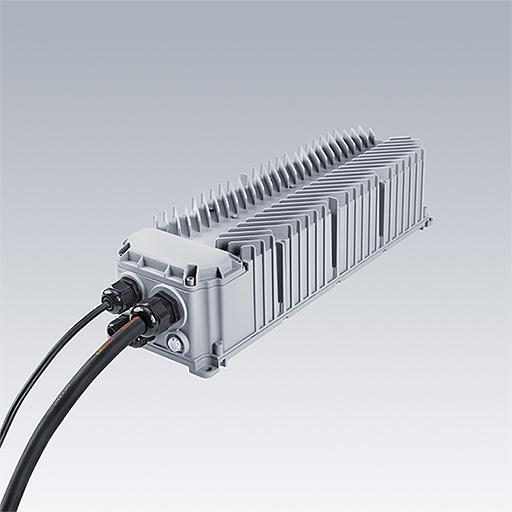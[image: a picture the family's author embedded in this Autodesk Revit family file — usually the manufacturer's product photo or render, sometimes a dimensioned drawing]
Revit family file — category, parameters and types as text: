
# Revit family: Thorn ALTIS GEN5 3 Modules
name_source: partatom
category: Lighting Fixtures
units: mm (PartAtom-declared; Revit-internal decimal feet)

## family parameters
Cut with Voids When Loaded = No
Host = Face
Light Source = No
Maintain Annotation Orientation = No
Part Type = Normal
Room Calculation Point = Yes
Round Connector Dimension = Use Diameter
Shared = No

## types (31) — shared parameters
Assembly Code = Pr_70_70_48_31
Connection Box Left Inside = No
Connection Box Left Outside = Yes
Connection Box Right Inside = No
Connection Box Right Outside = No
Description = Sports Floodlighting
Export Type to IFC As = IfcLightFixtureType
Gearbox = Yes
Initial Color Temperature = 4000
Lamp = LED
Luminaire Height = 685 mm
Luminaire Length = 530 mm  [stored 1.73885 ft]
Luminaire Width = 757 mm
Manufacturer = Zumtobel Lighting
Material = Thorn-Aluminium-RAL 7043-Traffic Grey B
Power Factor = 1
SELECT ACCESSORIES = SELECT CONNECTION BOX POSITION
SELECT CONNECTION BOX POSITION = SELECT CONNECTION BOX POSITION
SELECT GEARBOX TYPE = SELECT CONNECTION BOX POSITION
SELECT MODULE PROPERTIES = SELECT MODULE PROPERTIES
Type Gearbox = Thorn ALTIS GEN5 Gearbox-Premium-class C5 with NTC : ALG5 GB 1368W 1.40A 565V 2CH DA
Type IFC Predefined Type = DIRECTIONSOURCE
URL = https://www.thornlighting.com
zero-valued in all types: Default Elevation

## per-type parameters (varying)
| type | Apparent Load | Model | RGB Light Colours | Type Image | Wattage |
| ALG5 432L105-740 PST A6A6A6 ANT | 1366 VA | 96684127 | No | TLG_ALT5_F_V3_FIFA.jpg | 1366 W |
| ALG5 432L125-740 PST A6A6A6 ANT | 1639 VA | 96684126 | No | TLG_ALT5_F_V3_FIFA.jpg | 1639 W |
| ALG5 432L140-740 PST A6A6A6 ANT | 1873 VA | 96670248 | No | TLG_ALT5_F_V3_FIFA.jpg | 1873 W |
| ALG5 432L70-740 PST A6A6A6 ANT | 890 VA | 96684129 | No | TLG_ALT5_F_V3_FIFA.jpg | 890 W |
| ALG5 432L85-740 PST A6A6A6 ANT | 1093 VA | 96684128 | No | TLG_ALT5_F_V3_FIFA.jpg | 1093 W |
| ALG5 456L105-740 PST NBA6A6 ANT | 1444 VA | 96684131 | No | TLG_ALT5_F_V3_FIFA.jpg | 1444 W |
| ALG5 456L125-740 PST NBA6A6 ANT | 1732 VA | 96684130 | No | TLG_ALT5_F_V3_FIFA.jpg | 1732 W |
| ALG5 456L70-740 PST NBA6A6 ANT | 942 VA | 96684133 | No | TLG_ALT5_F_V3_FIFA.jpg | 942 W |
| ALG5 456L85-740 PST NBA6A6 ANT | 1157 VA | 96684132 | No | TLG_ALT5_F_V3_FIFA.jpg | 1157 W |
| ALG5 480L105-740 PST NBNBA6 ANT | 1517 VA | 96684135 | No | TLG_ALT5_F_V3_FIFA.jpg | 1517 W |
| ALG5 480L125-740 PST NBNBA6 ANT | 1820 VA | 96684134 | No | TLG_ALT5_F_V3_FIFA.jpg | 1820 W |
| ALG5 480L70-740 PST NBNBA6 ANT | 990 VA | 96684137 | No | TLG_ALT5_F_V3_FIFA.jpg | 990 W |
| ALG5 480L85-740 PST NBNBA6 ANT | 1216 VA | 96684136 | No | TLG_ALT5_F_V3_FIFA.jpg | 1216 W |
| ALG5 504L105-740 PST NBNBNB ANT | 1586 VA | 96684138 | No | TLG_ALT5_F_V3_FIFA.jpg | 1586 W |
| ALG5 504L125-740 PST NBNBNB ANT | 1902 VA | 96670249 | No | TLG_ALT5_F_V3_FIFA.jpg | 1902 W |
| ALG5 504L70-740 PST NBNBNB ANT | 1035 VA | 96684140 | No | TLG_ALT5_F_V3_FIFA.jpg | 1035 W |
| ALG5 504L85-740 PST NBNBNB ANT | 1270 VA | 96684139 | No | TLG_ALT5_F_V3_FIFA.jpg | 1270 W |
| ALG5 LE 432L105-740 PST A6A6A6 ANT | 1366 VA | 96637088 | No | TLG_ALT5_F_V3_FIFA.jpg | 1366 W |
| ALG5 LE 432L125-740 PST A6A6A6 ANT | 1639 VA | 96637087 | No | TLG_ALT5_F_V3_FIFA.jpg | 1639 W |
| ALG5 LE 432L140-740 PST A6A6A6 ANT | 1873 VA | 96800239 | No | TLG_ALT5_F_V3_FIFA.jpg | 1873 W |
| ALG5 LE 432L85-740 PST A6A6A6 ANT | 1093 VA | 96637089 | No | TLG_ALT5_F_V3_FIFA.jpg | 1093 W |
| ALG5 LE 456L105-740 PST NBA6A6 ANT | 1444 VA | 96637091 | No | TLG_ALT5_F_V3_FIFA.jpg | 1444 W |
| ALG5 LE 456L125-740 PST NBA6A6 ANT | 1732 VA | 96637090 | No | TLG_ALT5_F_V3_FIFA.jpg | 1732 W |
| ALG5 LE 456L85-740 PST NBA6A6 ANT | 1157 VA | 96637092 | No | TLG_ALT5_F_V3_FIFA.jpg | 1157 W |
| ALG5 LE 480L105-740 PST NBNBA6 ANT | 1517 VA | 96637094 | No | TLG_ALT5_F_V3_FIFA.jpg | 1517 W |
| ALG5 LE 480L125-740 PST NBNBA6 ANT | 1820 VA | 96637093 | No | TLG_ALT5_F_V3_FIFA.jpg | 1820 W |
| ALG5 LE 480L85-740 PST NBNBA6 ANT | 1216 VA | 96637095 | No | TLG_ALT5_F_V3_FIFA.jpg | 1216 W |
| ALG5 LE 504L105-740 PST NBNBNB ANT | 1586 VA | 96637097 | No | TLG_ALT5_F_V3_FIFA.jpg | 1586 W |
| ALG5 LE 504L125-740 PST NBNBNB ANT | 1902 VA | 96637096 | No | TLG_ALT5_F_V3_FIFA.jpg | 1902 W |
| ALG5 LE 504L85-740 PST NBNBNB ANT | 1270 VA | 96637098 | No | TLG_ALT5_F_V3_FIFA.jpg | 1270 W |
| ALG5 RGBW 396L85 B PAR NB NB NB ANT | 1022 VA | 96685676 | Yes | TLG_ALT5_F_V3_ANT_RGBW.jpg | 1022 W |

note: [stored X ft] marks values corroborated as IEEE doubles in the binary element streams (Revit-internal decimal feet)

## geometry (parser evidence)
native form markers: Sweep x15
no freeform markers — native parametric forms only
